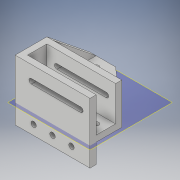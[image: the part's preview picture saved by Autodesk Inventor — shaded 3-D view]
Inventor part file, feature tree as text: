
AUTODESK INVENTOR PART (.ipt)
format: ipt  version: 2019 (Build 230136000, 136)  size: 208,896 bytes
history: native  units: in
note: dims shown in document units (in); Inventor stores cm internally (conversion verified against a paired STEP export)
features: extrude x7, sketch x7, plane x1, projected_geometry x1
ambient origin geometry x8: Origin, YZ Plane, XZ Plane, XY Plane, X Axis, Y Axis, Z Axis, Center Point
bodies: Solid1 (feature_tree)
feature tree (16):
  extrude  "Extrusion1"  Depth=0.7874in
  extrude  "Extrusion2"  Depth=0.25in
  extrude  "Extrusion3"  Depth=2.4528in TaperAngle=0.0deg
  plane  "Work Plane1"
  extrude  "Extrusion4"  Depth=0.7874in
  extrude  "Extrusion5"  Depth=0.3937in
  extrude  "Extrusion6"  Depth=0.3937in
  extrude  "Extrusion7"  Depth=0.25in
  sketch  "Sketch1"  dims[d0=2.0in d1=0.7874in]
  sketch  "Sketch2"  dims[d2=0.7874in d3=0.25in]
  sketch  "Sketch3"  dims[d4=0.25in d5=2.4528in d6=0.0in]
  sketch  "Sketch4"  dims[d7=0.7874in d8=0.2165in]
  projected_geometry  "Projected Loop1"
  sketch  "Sketch5"  dims[d9=0.75in d10=1.1811in d12=0.7687in d13=0.3937in d15=1.0in]
  sketch  "Sketch6"  dims[d17=2.4528in d18=0.0in d19=0.3937in]
  sketch  "Sketch7"  dims[d20=0.2165in d21=0.75in d22=1.1811in d24=0.7687in d25=0.3937in d27=1.0in d29=2.4528in d30=0.0in d31=-0.7874in d32=0.7874in d33=1.1811in d35=1.0in d36=0.3937in d38=1.0in d40=0.2165in d41=1.1811in d43=1.0in d44=0.3937in d46=1.0in d48=0.25in d49=0.0in d50=0.25in d51=0.25in d52=0.25in d53=0.0in d54=0.8268in d55=0.1969in d56=2.0in d57=0.25in d58=0.0in d59=0.25in d60=0.0in]
